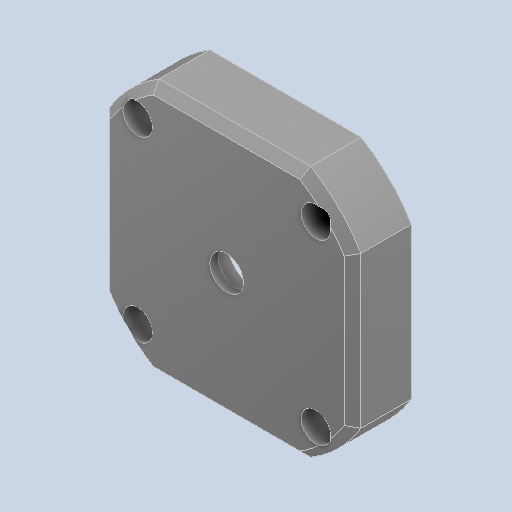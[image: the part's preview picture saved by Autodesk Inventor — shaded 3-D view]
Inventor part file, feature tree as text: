
AUTODESK INVENTOR PART (.ipt)
format: ipt  version: 2022 (Build 260153000, 153)  size: 161,280 bytes
history: mixed  units: in
note: dims shown in document units (in); Inventor stores cm internally (conversion verified against a paired STEP export)
features: chamfer x1, imported_body x1
ambient origin geometry x8: Origin, YZ Plane, XZ Plane, XY Plane, X Axis, Y Axis, Z Axis, Center Point
bodies: Solid1 (imported_parasolid)
feature tree (2):
  chamfer  "Chamfer2"  [1 undecoded]
  imported_body  NMx_Import_Brep_tag  [imported B-rep: ~30 faces, bbox_mm=[60.0, 60.0, 12.0]]
note: 1 required parameter value undecoded (feature->parameter linkage not recoverable at this tier; creation-order binding heuristic only, values carry confidence <= 0.55)
